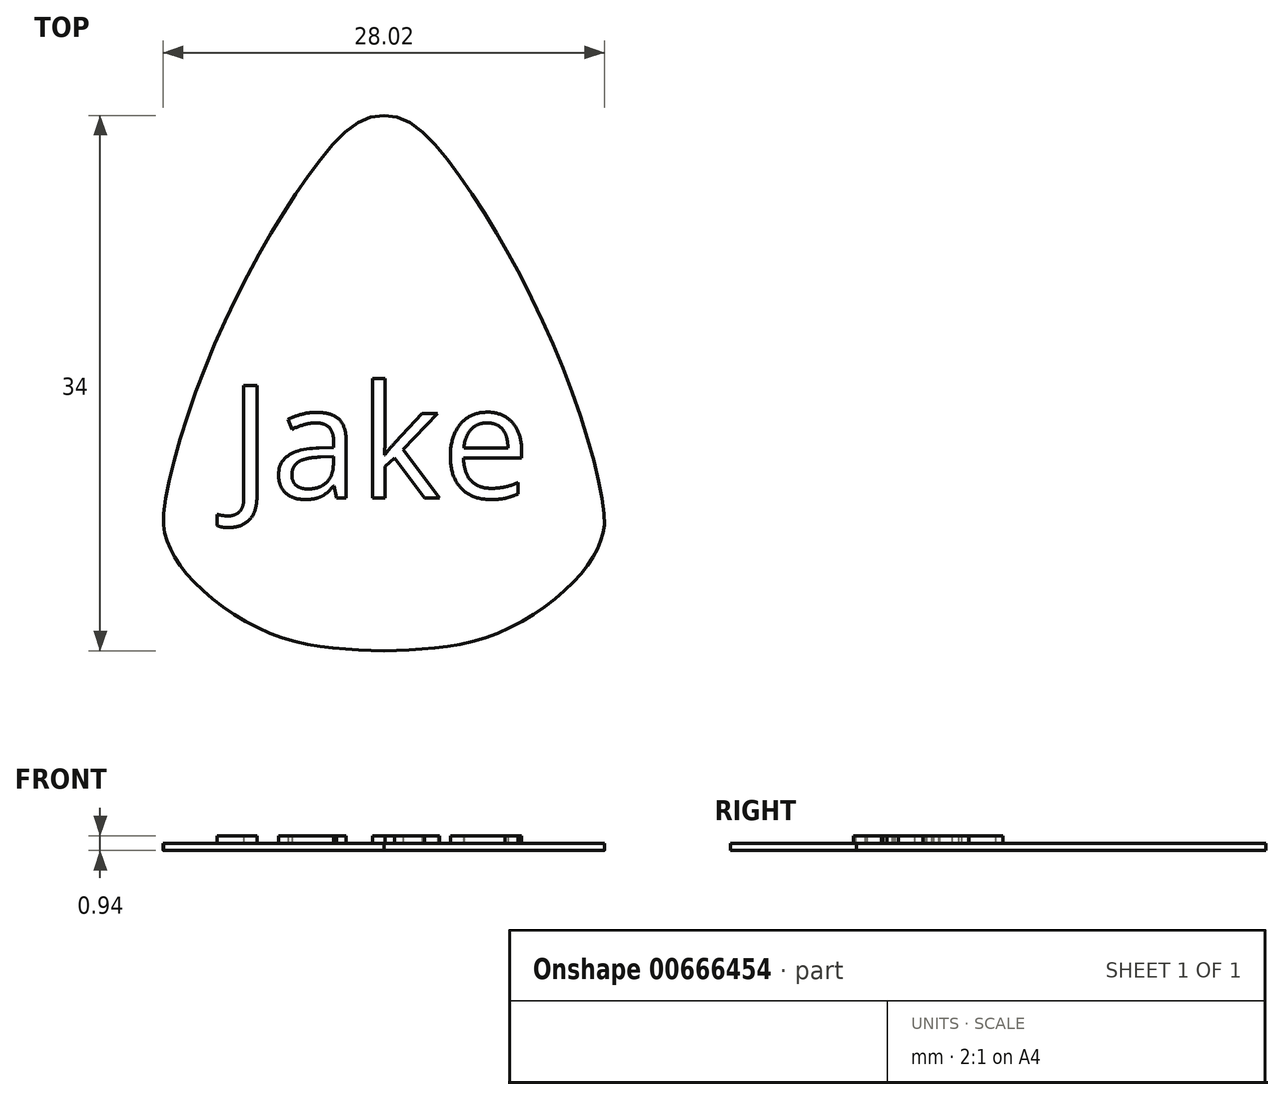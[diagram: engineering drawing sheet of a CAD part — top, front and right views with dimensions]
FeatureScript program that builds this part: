
annotation { "Feature Type Name" : "Feature", "Feature Type Description" : "" }
export const myFeature = defineFeature(function(context is Context, id is Id, definition is map)
    precondition{}
    {
        {
            var Q0;
            Q0=qCreatedBy(makeId("Top.planeOp"),FACE);
            var sketch = newSketch(context, id + "F0", { "sketchPlane" : qUnion([Q0])});
            skLineSegment(sketch, "E0", {"start": v(0, 0) * mm, "end": v(14, 0) * mm, "construction": true});
            skLineSegment(sketch, "E1", {"start": v(0, 0) * mm, "end": v(0, 26) * mm});
            skLineSegment(sketch, "E2", {"start": v(0, 0) * mm, "end": v(0, -8) * mm});
            skPoint(sketch, "E3.visualSharp", {"position": v(0, 26) * mm});
            skPoint(sketch, "E4.visualSharp", {"position": v(14, 0) * mm});
            skPoint(sketch, "E5.visualSharp", {"position": v(-14, 0) * mm});
            skPoint(sketch, "E6.visualSharp", {"position": v(0, -8) * mm});
            skFitSpline(sketch, "E7", {"points": [v(14, 0) * mm, v(11.62, 9.32) * mm, v(4.96, 21.93) * mm, v(0, 26) * mm], "startDerivative": vector(1.14, 13.58) * mm, "endDerivative": vector(-19.46, -1.2) * mm});
            skFitSpline(sketch, "E8", {"points": [v(0, -8) * mm, v(6.82, -7.05) * mm, v(12.52, -3.11) * mm, v(14, 0) * mm], "startDerivative": vector(18.55, 0.5) * mm, "endDerivative": vector(1.4, 11.8) * mm});
            skSolve(sketch);
        }
        {
            var Q0;
            Q0=makeQuery(id+"F0.imprint","IMPRINT",FACE,{"disambiguationData":[TD([[makeQuery(id+"F0.imprint","IMPRINT",EDGE,{"derivedFrom":sQuery(id+"F0.wireOp",EDGE,"E1")}),-1.0]])]});
            extrude(context, id + "F1", {"entities" : qUnion([Q0]), "depth" : .44 * mm});
        }
        {
            var Q0;
            Q0=makeQuery(id+"F1.opExtrude","SWEPT_BODY",BODY,{"disambiguationData":[OSD([sQuery(id+"F0.wireOp",EDGE,"E1"),sQuery(id+"F0.wireOp",EDGE,"E2"),sQuery(id+"F0.wireOp",EDGE,"E7"),sQuery(id+"F0.wireOp",EDGE,"E8")])]});
            var Q1;
            Q1=qCreatedBy(makeId("Right.planeOp"),FACE);
            mirror(context, id + "F2", {"operationType" : NewBodyOperationType.ADD, "entities" : qUnion([Q0]), "mirrorPlane" : qUnion([Q1])});
        }
        {
            var Q0;
            {var subQ0=makeQuery(id+"F1.opExtrude","CAP_FACE",FACE,{"disambiguationData":[OSD([sQuery(id+"F0.wireOp",EDGE,"E1"),sQuery(id+"F0.wireOp",EDGE,"E2"),sQuery(id+"F0.wireOp",EDGE,"E7"),sQuery(id+"F0.wireOp",EDGE,"E8")])],"isStart":false});Q0=makeQuery(id+"F2.boolean.opBoolean","MERGE",FACE,{"derivedFrom":[subQ0,makeQuery(id+"F2.opPattern","COPY",FACE,{"derivedFrom":subQ0,"instanceName":"1"})]});}
            var sketch = newSketch(context, id + "F3", { "sketchPlane" : qUnion([Q0])});
            skSolve(sketch);
        }
        {
            var Q0;
            {var subQ0=makeQuery(id+"F1.opExtrude","CAP_EDGE",EDGE,{"disambiguationData":[OSD([sQuery(id+"F0.wireOp",EDGE,"E7")])],"isStart":false});Q0=makeQuery(id+"F3.imprint","IMPRINT",FACE,{"disambiguationData":[TD([[makeQuery(id+"F3.imprint","IMPRINT",EDGE,{"derivedFrom":subQ0}),1.0]])]});}
            var sketch = newSketch(context, id + "F4", { "sketchPlane" : qUnion([Q0])});
            skText(sketch, "E9", { "text": "Jake\n", "fontName": "OpenSans-Regular.ttf"});
            const initialGuessF4  = {"E9": [-0.00982, 0.0017, 1, 0, 0.0072]};
            skSetInitialGuess(sketch, initialGuessF4);
            skSolve(sketch);
        }
        {
            var Q0;
            Q0 = qSketchRegion(id + "F4", true);
            extrude(context, id + "F5", {"entities" : qUnion([Q0]), "operationType" : NewBodyOperationType.ADD, "depth" : 0.5 * mm, "offsetDistance" : 25 * mm});
        }
    });
